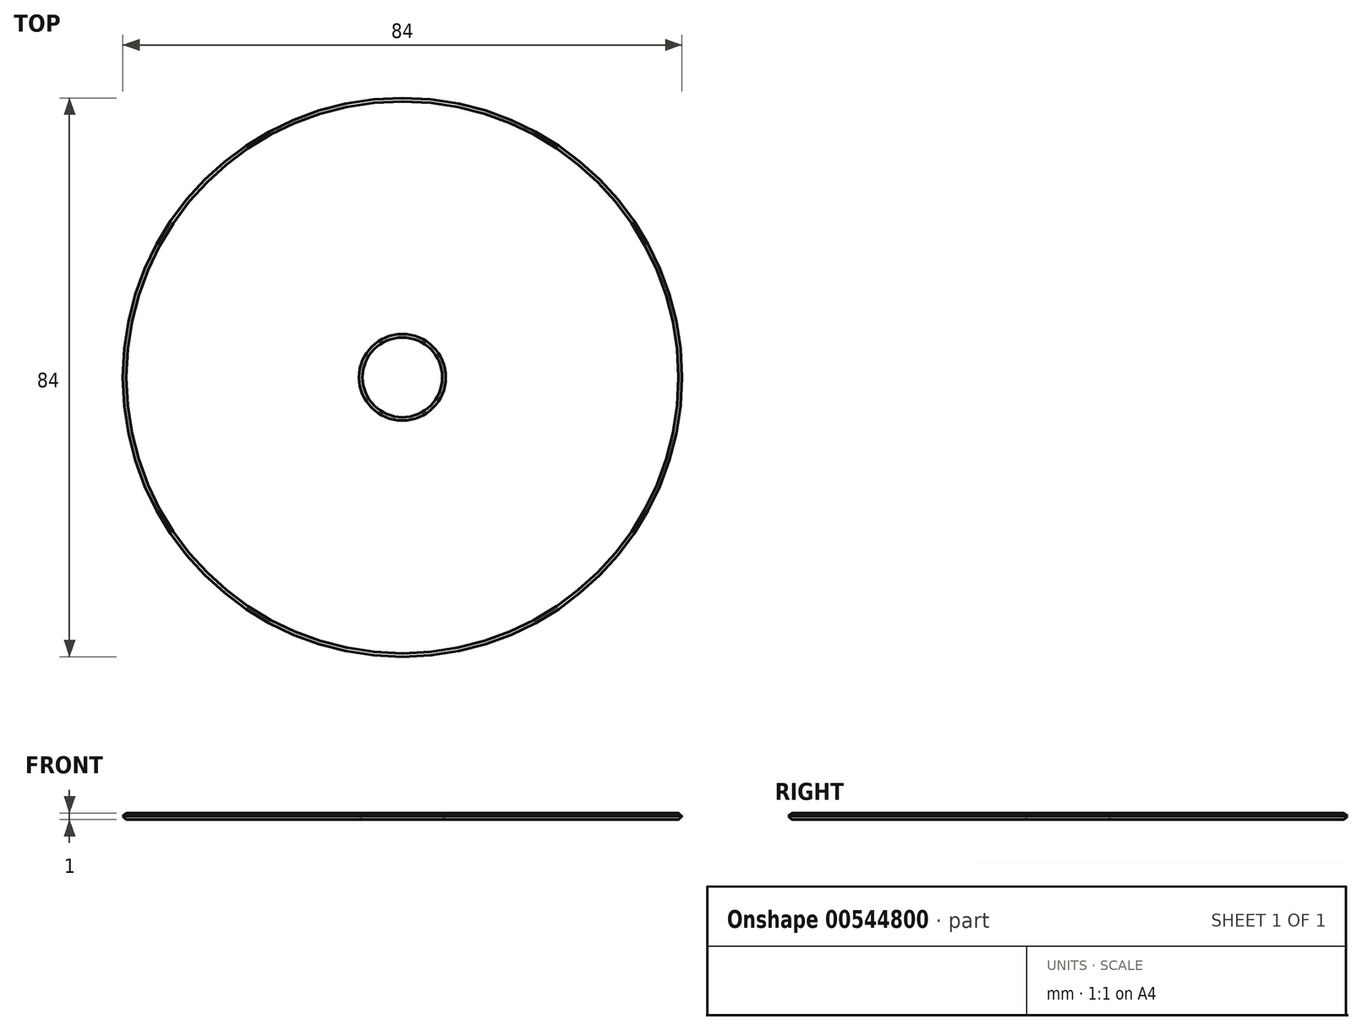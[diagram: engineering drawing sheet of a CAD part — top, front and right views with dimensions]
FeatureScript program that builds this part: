
annotation { "Feature Type Name" : "Feature", "Feature Type Description" : "" }
export const myFeature = defineFeature(function(context is Context, id is Id, definition is map)
    precondition{}
    {
        {
            var Q0;
            Q0=qCreatedBy(makeId("Top.planeOp"),FACE);
            var sketch = newSketch(context, id + "F0", { "sketchPlane" : qUnion([Q0])});
            skCircle(sketch, "E0", {"center": v(0, 0) * mm, "radius": 42 * mm});
            skCircle(sketch, "E1", {"center": v(0, 0) * mm, "radius": 6 * mm});
            skSolve(sketch);
        }
        {
            var Q0;
            Q0=makeQuery(id+"F0.imprint","IMPRINT",FACE,{"disambiguationData":[TD([[makeQuery(id+"F0.imprint","IMPRINT",EDGE,{"derivedFrom":sQuery(id+"F0.wireOp",EDGE,"E0")}),1.0]])]});
            extrude(context, id + "F1", {"entities" : qUnion([Q0]), "depth" : 1 * mm, "offsetDistance" : 25 * mm});
        }
        {
            var Q0;
            Q0=makeQuery(id+"F1.opExtrude","CAP_EDGE",EDGE,{"disambiguationData":[OSD([sQuery(id+"F0.wireOp",EDGE,"E1")])],"isStart":false});
            var Q1;
            Q1=makeQuery(id+"F1.opExtrude","CAP_EDGE",EDGE,{"disambiguationData":[OSD([sQuery(id+"F0.wireOp",EDGE,"E0")])],"isStart":false});
            var Q2;
            Q2=makeQuery(id+"F1.opExtrude","CAP_EDGE",EDGE,{"disambiguationData":[OSD([sQuery(id+"F0.wireOp",EDGE,"E0")])],"isStart":true});
            var Q3;
            Q3=makeQuery(id+"F1.opExtrude","CAP_EDGE",EDGE,{"disambiguationData":[OSD([sQuery(id+"F0.wireOp",EDGE,"E1")])],"isStart":true});
            chamfer(context, id + "F2", {"entities" : qUnion([Q0, Q1, Q2, Q3]), "width" : .5 * mm, "tangentPropagation" : true});
        }
    });
